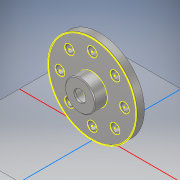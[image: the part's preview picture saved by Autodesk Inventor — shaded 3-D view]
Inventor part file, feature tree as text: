
AUTODESK INVENTOR PART (.ipt)
format: ipt  version: 2022 (Build 260153000, 153)  size: 194,048 bytes
history: mixed  units: mm
features: chamfer x2, sketch x1, projected_geometry x1, imported_body x1
ambient origin geometry x8: Origin, YZ Plane, XZ Plane, XY Plane, X Axis, Y Axis, Z Axis, Center Point
bodies: Solid1 (imported_parasolid), Solid2 (imported_parasolid)
feature tree (5):
  sketch  "Эскиз1"
  projected_geometry  "Спроецированная петля1"
  chamfer  "Chamfer2"  [1 undecoded]
  chamfer  "Chamfer5"  [1 undecoded]
  imported_body  NMx_Import_Brep_tag  [imported B-rep: ~28 faces, bbox_mm=[19.0, 16.0, 5.0]]
note: 2 required parameter values undecoded (feature->parameter linkage not recoverable at this tier; creation-order binding heuristic only, values carry confidence <= 0.55)
